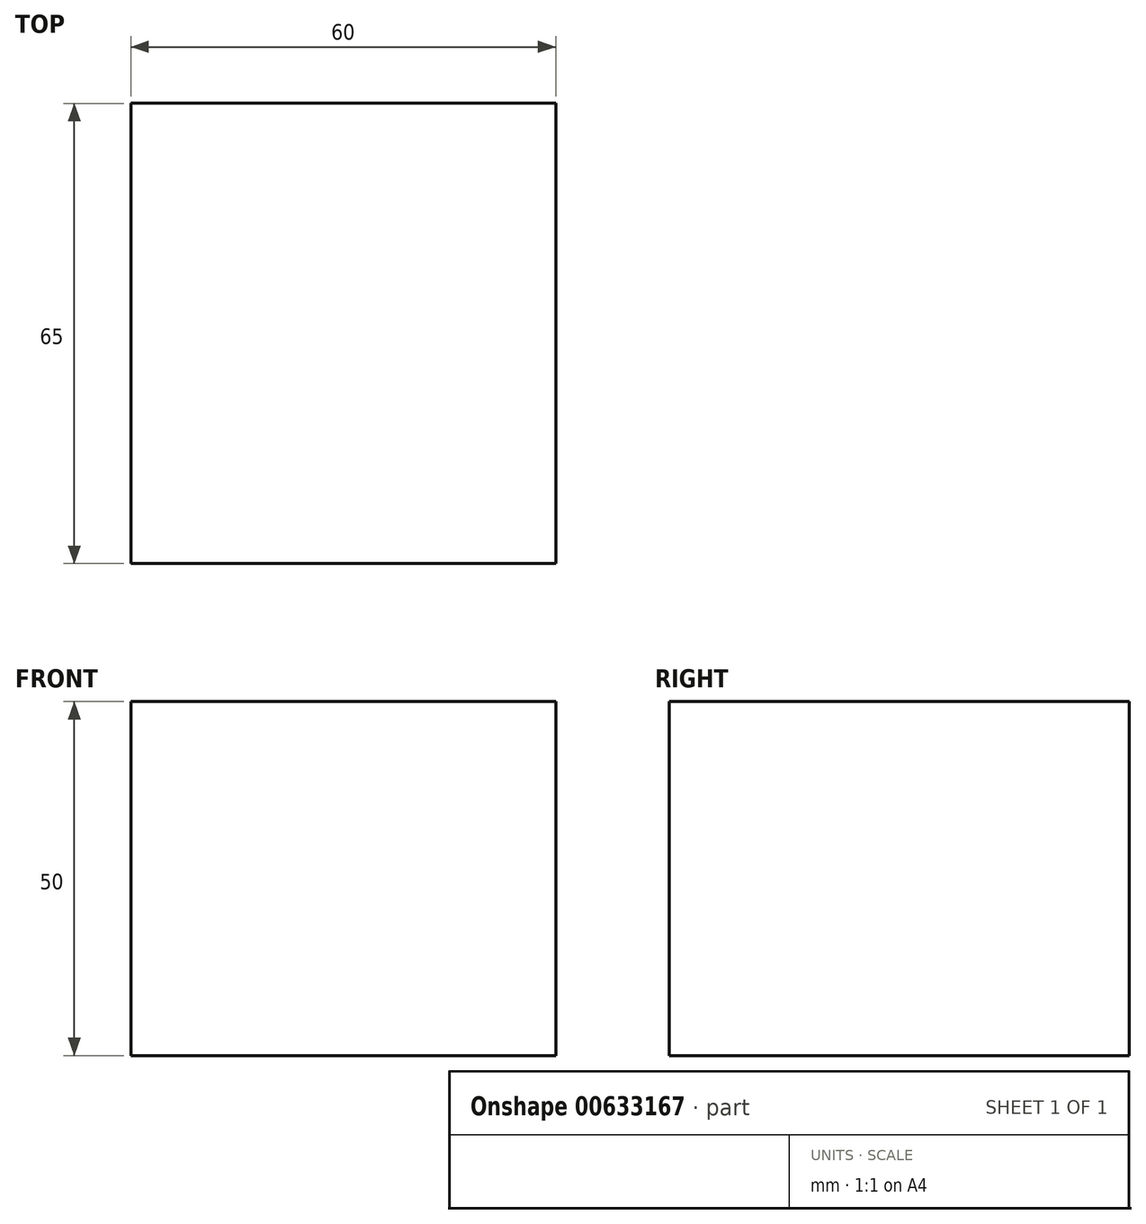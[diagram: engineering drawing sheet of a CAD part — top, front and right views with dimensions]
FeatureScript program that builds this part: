
annotation { "Feature Type Name" : "Feature", "Feature Type Description" : "" }
export const myFeature = defineFeature(function(context is Context, id is Id, definition is map)
    precondition{}
    {
        {
            var Q0;
            Q0=qCreatedBy(makeId("Top.planeOp"),FACE);
            var sketch = newSketch(context, id + "F0", { "sketchPlane" : qUnion([Q0])});
            skLineSegment(sketch, "E0.bottom", {"start": v(-27.58, 26.75) * mm, "end": v(32.42, 26.75) * mm});
            skLineSegment(sketch, "E0.top", {"start": v(-27.58, -38.25) * mm, "end": v(32.42, -38.25) * mm});
            skLineSegment(sketch, "E0.left", {"start": v(-27.58, 26.75) * mm, "end": v(-27.58, -38.25) * mm});
            skLineSegment(sketch, "E0.right", {"start": v(32.42, 26.75) * mm, "end": v(32.42, -38.25) * mm});
            skSolve(sketch);
        }
        {
            var Q0;
            Q0=makeQuery(id+"F0.imprint","IMPRINT",FACE,{"disambiguationData":[TD([[makeQuery(id+"F0.imprint","IMPRINT",EDGE,{"derivedFrom":sQuery(id+"F0.wireOp",EDGE,"E0.bottom")}),-1.0]])]});
            extrude(context, id + "F1", {"entities" : qUnion([Q0]), "depth" : 50 * mm, "offsetDistance" : 25 * mm});
        }
    });
